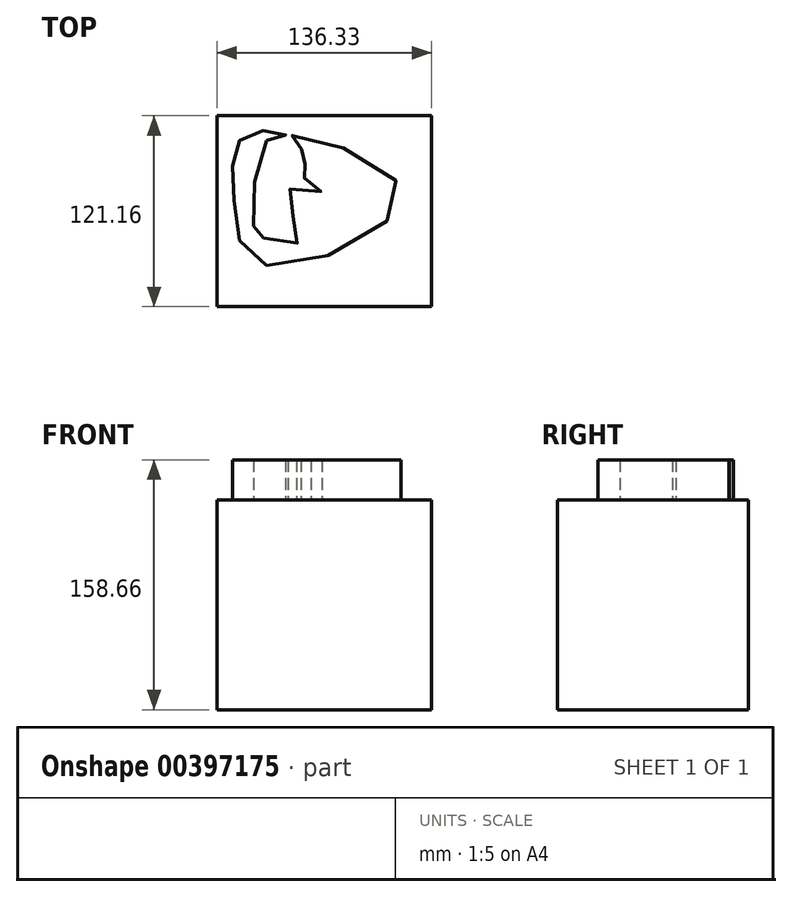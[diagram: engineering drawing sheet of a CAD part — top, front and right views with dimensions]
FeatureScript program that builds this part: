
annotation { "Feature Type Name" : "Feature", "Feature Type Description" : "" }
export const myFeature = defineFeature(function(context is Context, id is Id, definition is map)
    precondition{}
    {
        {
            var Q0;
            Q0=qCreatedBy(makeId("Front.planeOp"),FACE);
            var sketch = newSketch(context, id + "F0", { "sketchPlane" : qUnion([Q0])});
            skLineSegment(sketch, "E0.bottom", {"start": v(-66.8, 62.44) * mm, "end": v(69.52, 62.44) * mm});
            skLineSegment(sketch, "E0.top", {"start": v(-66.8, -70.82) * mm, "end": v(69.52, -70.82) * mm});
            skLineSegment(sketch, "E0.left", {"start": v(-66.8, 62.44) * mm, "end": v(-66.8, -70.82) * mm});
            skLineSegment(sketch, "E0.right", {"start": v(69.52, 62.44) * mm, "end": v(69.52, -70.82) * mm});
            skSolve(sketch);
        }
        {
            var Q0;
            Q0=makeQuery(id+"F0.imprint","IMPRINT",FACE,{"disambiguationData":[TD([[makeQuery(id+"F0.imprint","IMPRINT",EDGE,{"derivedFrom":sQuery(id+"F0.wireOp",EDGE,"E0.bottom")}),-1.0]])]});
            extrude(context, id + "F1", {"entities" : qUnion([Q0]), "depth" : 121.16 * mm});
        }
        {
            var Q0;
            Q0=makeQuery(id+"F1.opExtrude","SWEPT_FACE",FACE,{"disambiguationData":[OSD([sQuery(id+"F0.wireOp",EDGE,"E0.bottom")])]});
            var sketch = newSketch(context, id + "F2", { "sketchPlane" : qUnion([Q0])});
            skFitSpline(sketch, "E1", {"points": [v(-35.34, -15.74) * mm, v(-43.54, -72.02) * mm, v(-41.74, -75.73) * mm, v(-13.89, -79.32) * mm, v(-22.63, -47.74) * mm, v(0, -48.02) * mm, v(-16.35, -33.95) * mm, v(-6.98, -27.86) * mm, v(-21.8, -13.35) * mm, v(49.68, -46.7) * mm, v(-36.11, -94.87) * mm, v(-55.77, -56.7) * mm, v(-55.7, -22.75) * mm, v(-42.54, -9.73) * mm, v(-23.19, -12.12) * mm, v(-35.34, -15.74) * mm]});
            skSolve(sketch);
        }
        {
            var Q0;
            Q0 = qSketchRegion(id + "F2", true);
            extrude(context, id + "F3", {"entities" : qUnion([Q0]), "operationType" : NewBodyOperationType.ADD, "depth" : 25.4 * mm});
        }
    });
